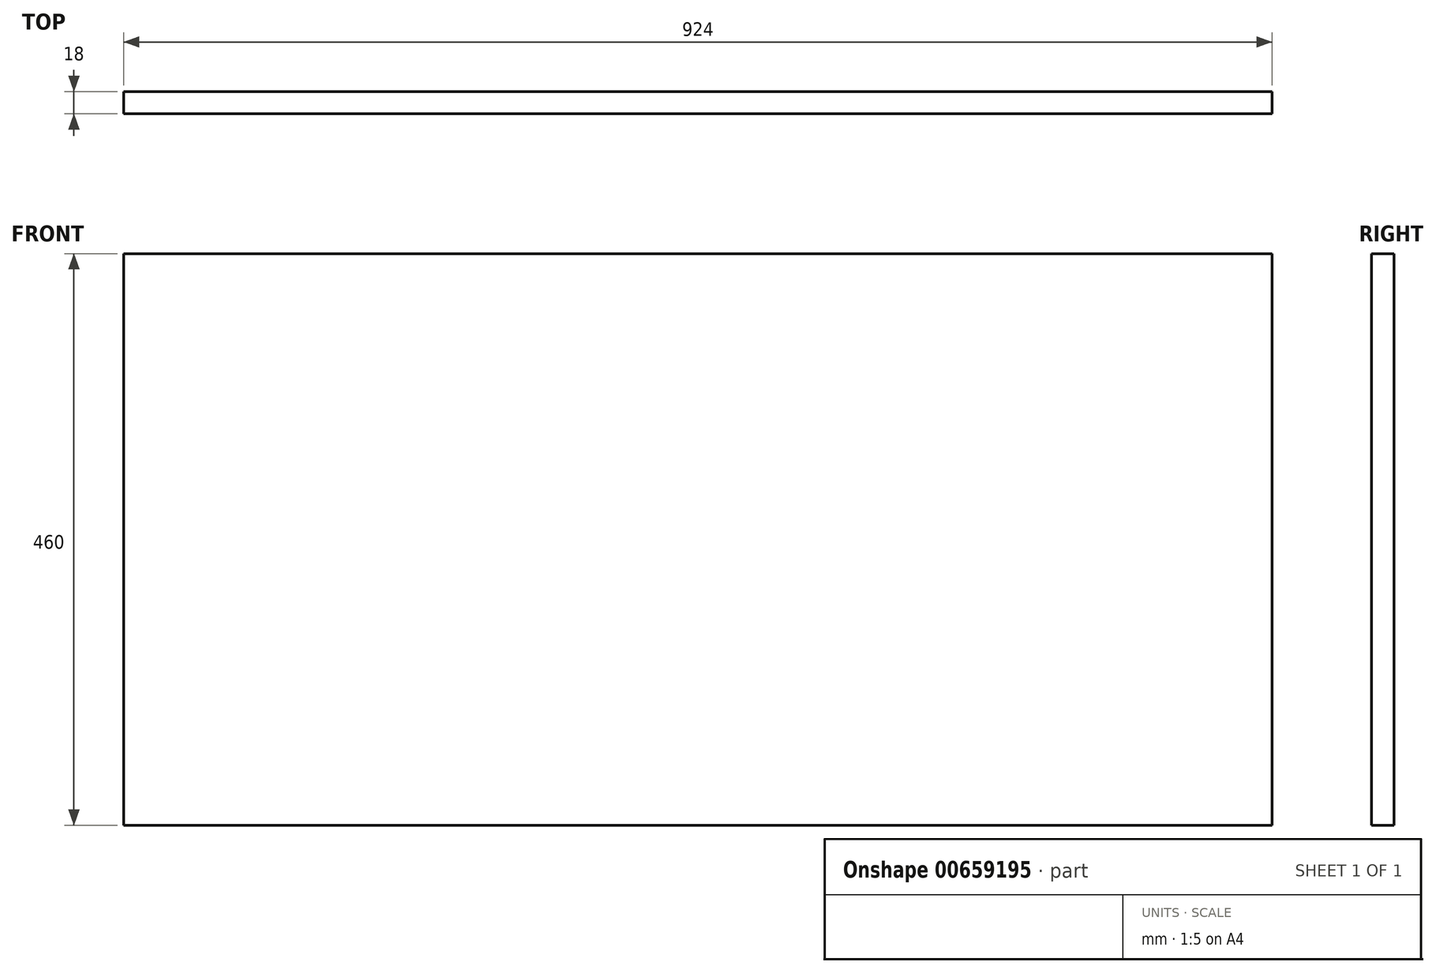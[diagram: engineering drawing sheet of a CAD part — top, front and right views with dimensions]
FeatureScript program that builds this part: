
annotation { "Feature Type Name" : "Feature", "Feature Type Description" : "" }
export const myFeature = defineFeature(function(context is Context, id is Id, definition is map)
    precondition{}
    {
        {
            var Q0;
            Q0=qCreatedBy(makeId("Front.planeOp"),FACE);
            var sketch = newSketch(context, id + "F0", { "sketchPlane" : qUnion([Q0])});
            skLineSegment(sketch, "E0.bottom", {"start": v(-462, -230) * mm, "end": v(462, -230) * mm});
            skLineSegment(sketch, "E0.top", {"start": v(-462, 230) * mm, "end": v(462, 230) * mm});
            skLineSegment(sketch, "E0.left", {"start": v(-462, -230) * mm, "end": v(-462, 230) * mm});
            skLineSegment(sketch, "E0.right", {"start": v(462, -230) * mm, "end": v(462, 230) * mm});
            skPoint(sketch, "E0.middle", {"position": v(0, 0) * mm});
            skSolve(sketch);
        }
        {
            var Q0;
            Q0=makeQuery(id+"F0.imprint","IMPRINT",FACE,{"disambiguationData":[TD([[makeQuery(id+"F0.imprint","IMPRINT",EDGE,{"derivedFrom":sQuery(id+"F0.wireOp",EDGE,"E0.bottom")}),1.0]])]});
            extrude(context, id + "F1", {"entities" : qUnion([Q0]), "endBound" : BoundingType.SYMMETRIC, "depth" : 18 * mm, "offsetDistance" : 25 * mm});
        }
    });
